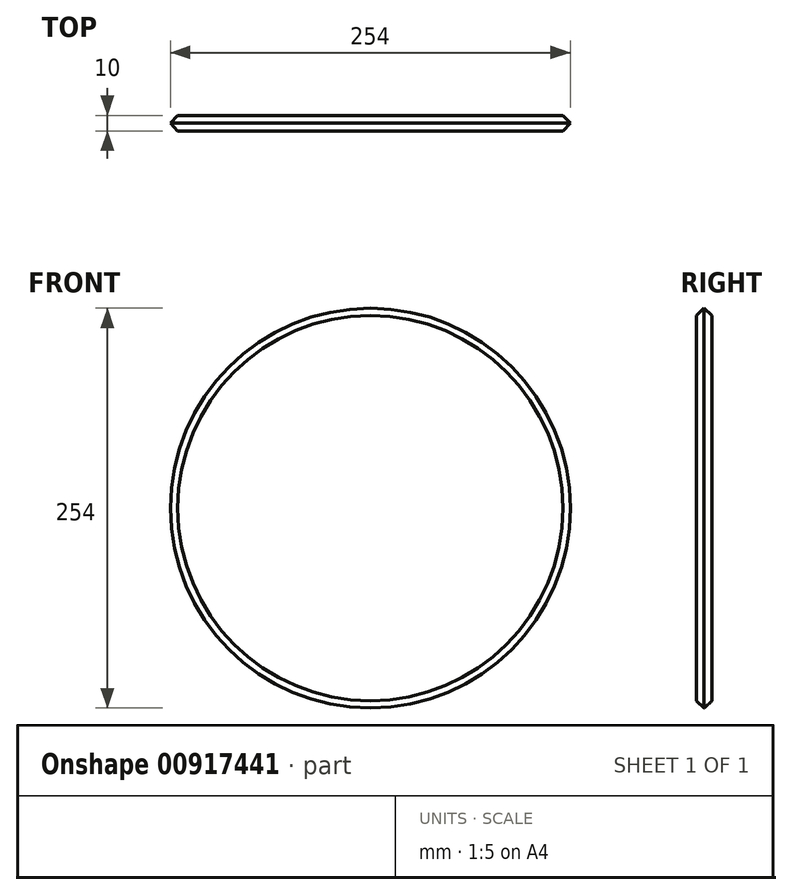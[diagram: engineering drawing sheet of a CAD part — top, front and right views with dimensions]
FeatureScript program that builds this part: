
annotation { "Feature Type Name" : "Feature", "Feature Type Description" : "" }
export const myFeature = defineFeature(function(context is Context, id is Id, definition is map)
    precondition{}
    {
        {
            var Q0;
            Q0=qCreatedBy(makeId("Front.planeOp"),FACE);
            var sketch = newSketch(context, id + "F0", { "sketchPlane" : qUnion([Q0])});
            skCircle(sketch, "E0", {"center": v(0, 0) * mm, "radius": 5 * mm});
            skCircle(sketch, "E1", {"center": v(0, 0) * mm, "radius": 127 * mm});
            skSolve(sketch);
        }
        {
            var Q0;
            Q0=makeQuery(id+"F0.imprint","IMPRINT",FACE,{"disambiguationData":[TD([[makeQuery(id+"F0.imprint","IMPRINT",EDGE,{"derivedFrom":sQuery(id+"F0.wireOp",EDGE,"E0")}),-1.0]])]});
            extrude(context, id + "F1", {"entities" : qUnion([Q0]), "oppositeDirection" : true, "depth" : 10 * mm, "offsetDistance" : 25.4 * mm, "symmetric" : true});
        }
        {
            var Q0;
            Q0=makeQuery(id+"F0.imprint","IMPRINT",FACE,{"disambiguationData":[TD([[makeQuery(id+"F0.imprint","IMPRINT",EDGE,{"derivedFrom":sQuery(id+"F0.wireOp",EDGE,"E0")}),1.0]])]});
            extrude(context, id + "F2", {"entities" : qUnion([Q0]), "operationType" : NewBodyOperationType.ADD, "depth" : 10 * mm, "offsetDistance" : 25 * mm, "symmetric" : true});
        }
        {
            var Q0;
            Q0=makeQuery(id+"F1.opExtrude","CAP_EDGE",EDGE,{"disambiguationData":[OSD([sQuery(id+"F0.wireOp",EDGE,"E1")])],"isStart":false});
            var Q1;
            Q1=makeQuery(id+"F1.opExtrude","CAP_EDGE",EDGE,{"disambiguationData":[OSD([sQuery(id+"F0.wireOp",EDGE,"E1")])],"isStart":true});
            chamfer(context, id + "F3", {"entities" : qUnion([Q0, Q1]), "chamferType" : ChamferType.OFFSET_ANGLE, "width" : 5 * mm, "oppositeDirection" : false, "angle" : 43 * degree, "tangentPropagation" : true});
        }
    });
